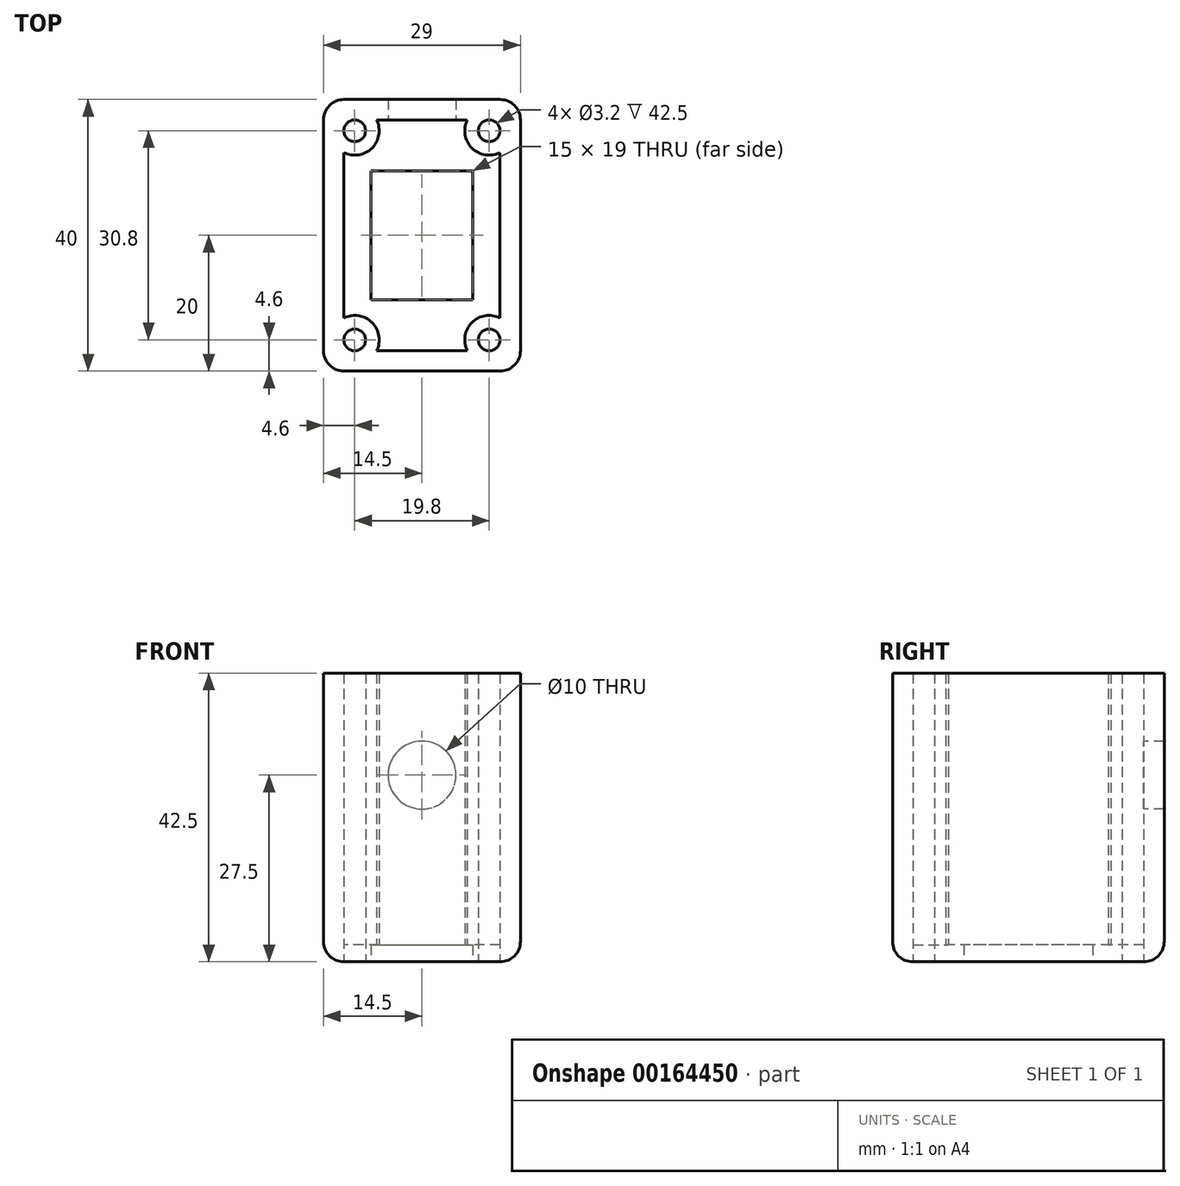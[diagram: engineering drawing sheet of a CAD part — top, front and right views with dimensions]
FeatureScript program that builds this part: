
annotation { "Feature Type Name" : "Feature", "Feature Type Description" : "" }
export const myFeature = defineFeature(function(context is Context, id is Id, definition is map)
    precondition{}
    {
        {
            var Q0;
            Q0=qCreatedBy(makeId("Top.planeOp"),FACE);
            var sketch = newSketch(context, id + "F0", { "sketchPlane" : qUnion([Q0])});
            skLineSegment(sketch, "E0.bottom", {"start": v(-14.5, 20) * mm, "end": v(14.5, 20) * mm});
            skLineSegment(sketch, "E0.top", {"start": v(-14.5, -20) * mm, "end": v(14.5, -20) * mm});
            skLineSegment(sketch, "E0.left", {"start": v(-14.5, 20) * mm, "end": v(-14.5, -20) * mm});
            skLineSegment(sketch, "E0.right", {"start": v(14.5, 20) * mm, "end": v(14.5, -20) * mm});
            skPoint(sketch, "E1", {"position": v(0, 20) * mm});
            skPoint(sketch, "E2", {"position": v(14.5, 0) * mm});
            skLineSegment(sketch, "E3.bottom", {"start": v(-7.5, 9.5) * mm, "end": v(7.5, 9.5) * mm});
            skLineSegment(sketch, "E3.top", {"start": v(-7.5, -9.5) * mm, "end": v(7.5, -9.5) * mm});
            skLineSegment(sketch, "E3.left", {"start": v(-7.5, 9.5) * mm, "end": v(-7.5, -9.5) * mm});
            skLineSegment(sketch, "E3.right", {"start": v(7.5, 9.5) * mm, "end": v(7.5, -9.5) * mm});
            skPoint(sketch, "E4", {"position": v(0, 9.5) * mm});
            skPoint(sketch, "E5", {"position": v(-7.5, 0) * mm});
            skSolve(sketch);
        }
        {
            var Q0;
            Q0=makeQuery(id+"F0.imprint","IMPRINT",FACE,{"disambiguationData":[TD([[makeQuery(id+"F0.imprint","IMPRINT",EDGE,{"derivedFrom":sQuery(id+"F0.wireOp",EDGE,"E0.bottom")}),-1.0]])]});
            extrude(context, id + "F1", {"entities" : qUnion([Q0]), "depth" : 2.5 * mm});
        }
        {
            var Q0;
            Q0=makeQuery(id+"F1.opExtrude","CAP_FACE",FACE,{"disambiguationData":[OSD([sQuery(id+"F0.wireOp",EDGE,"E0.bottom"),sQuery(id+"F0.wireOp",EDGE,"E0.top"),sQuery(id+"F0.wireOp",EDGE,"E0.left"),sQuery(id+"F0.wireOp",EDGE,"E0.right"),sQuery(id+"F0.wireOp",EDGE,"E3.bottom"),sQuery(id+"F0.wireOp",EDGE,"E3.top"),sQuery(id+"F0.wireOp",EDGE,"E3.left"),sQuery(id+"F0.wireOp",EDGE,"E3.right")])],"isStart":false});
            var sketch = newSketch(context, id + "F2", { "sketchPlane" : qUnion([Q0])});
            skLineSegment(sketch, "E6.bottom", {"start": v(-11.5, 17) * mm, "end": v(11.5, 17) * mm});
            skLineSegment(sketch, "E6.top", {"start": v(-11.5, -17) * mm, "end": v(11.5, -17) * mm});
            skLineSegment(sketch, "E6.left", {"start": v(-11.5, 17) * mm, "end": v(-11.5, -17) * mm});
            skLineSegment(sketch, "E6.right", {"start": v(11.5, 17) * mm, "end": v(11.5, -17) * mm});
            skSolve(sketch);
        }
        {
            var Q0;
            Q0=makeQuery(id+"F2.imprint","IMPRINT",FACE,{"disambiguationData":[TD([[makeQuery(id+"F2.imprint","IMPRINT",EDGE,{"derivedFrom":sQuery(id+"F2.wireOp",EDGE,"E6.bottom")}),1.0]])]});
            extrude(context, id + "F3", {"entities" : qUnion([Q0]), "operationType" : NewBodyOperationType.ADD, "depth" : 40 * mm});
        }
        {
            var Q0;
            Q0=makeQuery(id+"F1.opExtrude","CAP_FACE",FACE,{"disambiguationData":[OSD([sQuery(id+"F0.wireOp",EDGE,"E0.bottom"),sQuery(id+"F0.wireOp",EDGE,"E0.top"),sQuery(id+"F0.wireOp",EDGE,"E0.left"),sQuery(id+"F0.wireOp",EDGE,"E0.right"),sQuery(id+"F0.wireOp",EDGE,"E3.bottom"),sQuery(id+"F0.wireOp",EDGE,"E3.top"),sQuery(id+"F0.wireOp",EDGE,"E3.left"),sQuery(id+"F0.wireOp",EDGE,"E3.right")])],"isStart":false});
            var sketch = newSketch(context, id + "F4", { "sketchPlane" : qUnion([Q0])});
            skCircle(sketch, "E7", {"center": v(-9.9, 15.4) * mm, "radius": 3.6 * mm});
            skCircle(sketch, "E8", {"center": v(9.9, 15.4) * mm, "radius": 3.6 * mm});
            skCircle(sketch, "E9", {"center": v(9.9, -15.4) * mm, "radius": 3.6 * mm});
            skCircle(sketch, "E10", {"center": v(-9.9, -15.4) * mm, "radius": 3.6 * mm});
            skCircle(sketch, "E11", {"center": v(-9.9, 15.4) * mm, "radius": 1.6 * mm});
            skCircle(sketch, "E12", {"center": v(9.9, 15.4) * mm, "radius": 1.6 * mm});
            skCircle(sketch, "E13", {"center": v(-9.9, -15.4) * mm, "radius": 1.6 * mm});
            skCircle(sketch, "E14", {"center": v(9.9, -15.4) * mm, "radius": 1.6 * mm});
            skSolve(sketch);
        }
        {
            var Q0;
            {var subQ0=sQuery(id+"F4.wireOp",EDGE,"E7");var subQ1=makeQuery(id+"F3.opExtrude","CAP_EDGE",EDGE,{"disambiguationData":[OSD([sQuery(id+"F2.wireOp",EDGE,"E6.bottom")])],"isStart":true});var subQ2=makeQuery(id+"F4.imprint","INTERSECT",VERTEX,{"derivedFrom":[subQ1,subQ0]});Q0=makeQuery(id+"F4.imprint","IMPRINT",FACE,{"disambiguationData":[TD([[makeQuery(id+"F4.imprint","IMPRINT",EDGE,{"disambiguationData":[TD([[subQ2,1.0]])],"derivedFrom":subQ0}),1.0]])]});}
            var Q1;
            {var subQ0=sQuery(id+"F4.wireOp",EDGE,"E11");var subQ1=makeQuery(id+"F3.opExtrude","CAP_EDGE",EDGE,{"disambiguationData":[OSD([sQuery(id+"F2.wireOp",EDGE,"E6.bottom")])],"isStart":true});var subQ2=makeQuery(id+"F4.imprint","INTERSECT",VERTEX,{"derivedFrom":[subQ1,subQ0]});Q1=makeQuery(id+"F4.imprint","IMPRINT",FACE,{"disambiguationData":[TD([[makeQuery(id+"F4.imprint","IMPRINT",EDGE,{"disambiguationData":[TD([[subQ2,-1.0]])],"derivedFrom":subQ0}),-1.0]])]});}
            var Q2;
            {var subQ0=sQuery(id+"F4.wireOp",EDGE,"E8");var subQ1=makeQuery(id+"F3.opExtrude","CAP_EDGE",EDGE,{"disambiguationData":[OSD([sQuery(id+"F2.wireOp",EDGE,"E6.bottom")])],"isStart":true});var subQ2=makeQuery(id+"F4.imprint","INTERSECT",VERTEX,{"derivedFrom":[subQ1,subQ0]});Q2=makeQuery(id+"F4.imprint","IMPRINT",FACE,{"disambiguationData":[TD([[makeQuery(id+"F4.imprint","IMPRINT",EDGE,{"disambiguationData":[TD([[subQ2,-1.0]])],"derivedFrom":subQ0}),1.0]])]});}
            var Q3;
            {var subQ0=sQuery(id+"F4.wireOp",EDGE,"E12");var subQ1=makeQuery(id+"F3.opExtrude","CAP_EDGE",EDGE,{"disambiguationData":[OSD([sQuery(id+"F2.wireOp",EDGE,"E6.bottom")])],"isStart":true});var subQ2=makeQuery(id+"F4.imprint","INTERSECT",VERTEX,{"derivedFrom":[subQ1,subQ0]});Q3=makeQuery(id+"F4.imprint","IMPRINT",FACE,{"disambiguationData":[TD([[makeQuery(id+"F4.imprint","IMPRINT",EDGE,{"disambiguationData":[TD([[subQ2,1.0]])],"derivedFrom":subQ0}),-1.0]])]});}
            var Q4;
            {var subQ0=sQuery(id+"F4.wireOp",EDGE,"E13");var subQ1=makeQuery(id+"F3.opExtrude","CAP_EDGE",EDGE,{"disambiguationData":[OSD([sQuery(id+"F2.wireOp",EDGE,"E6.top")])],"isStart":true});var subQ2=makeQuery(id+"F4.imprint","INTERSECT",VERTEX,{"derivedFrom":[subQ1,subQ0]});Q4=makeQuery(id+"F4.imprint","IMPRINT",FACE,{"disambiguationData":[TD([[makeQuery(id+"F4.imprint","IMPRINT",EDGE,{"disambiguationData":[TD([[subQ2,1.0]])],"derivedFrom":subQ0}),-1.0]])]});}
            var Q5;
            {var subQ0=sQuery(id+"F4.wireOp",EDGE,"E10");var subQ1=makeQuery(id+"F3.opExtrude","CAP_EDGE",EDGE,{"disambiguationData":[OSD([sQuery(id+"F2.wireOp",EDGE,"E6.top")])],"isStart":true});var subQ2=makeQuery(id+"F4.imprint","INTERSECT",VERTEX,{"derivedFrom":[subQ1,subQ0]});Q5=makeQuery(id+"F4.imprint","IMPRINT",FACE,{"disambiguationData":[TD([[makeQuery(id+"F4.imprint","IMPRINT",EDGE,{"disambiguationData":[TD([[subQ2,-1.0]])],"derivedFrom":subQ0}),1.0]])]});}
            var Q6;
            {var subQ0=sQuery(id+"F4.wireOp",EDGE,"E9");var subQ1=makeQuery(id+"F3.opExtrude","CAP_EDGE",EDGE,{"disambiguationData":[OSD([sQuery(id+"F2.wireOp",EDGE,"E6.top")])],"isStart":true});var subQ2=makeQuery(id+"F4.imprint","INTERSECT",VERTEX,{"derivedFrom":[subQ1,subQ0]});Q6=makeQuery(id+"F4.imprint","IMPRINT",FACE,{"disambiguationData":[TD([[makeQuery(id+"F4.imprint","IMPRINT",EDGE,{"disambiguationData":[TD([[subQ2,1.0]])],"derivedFrom":subQ0}),1.0]])]});}
            var Q7;
            {var subQ0=sQuery(id+"F4.wireOp",EDGE,"E14");var subQ1=makeQuery(id+"F3.opExtrude","CAP_EDGE",EDGE,{"disambiguationData":[OSD([sQuery(id+"F2.wireOp",EDGE,"E6.top")])],"isStart":true});var subQ2=makeQuery(id+"F4.imprint","INTERSECT",VERTEX,{"derivedFrom":[subQ1,subQ0]});Q7=makeQuery(id+"F4.imprint","IMPRINT",FACE,{"disambiguationData":[TD([[makeQuery(id+"F4.imprint","IMPRINT",EDGE,{"disambiguationData":[TD([[subQ2,-1.0]])],"derivedFrom":subQ0}),-1.0]])]});}
            var Q8;
            Q8=makeQuery(id+"F3.opExtrude","CAP_FACE",FACE,{"disambiguationData":[OSD([sQuery(id+"F0.wireOp",EDGE,"E0.bottom"),sQuery(id+"F0.wireOp",EDGE,"E0.top"),sQuery(id+"F0.wireOp",EDGE,"E0.left"),sQuery(id+"F0.wireOp",EDGE,"E0.right"),sQuery(id+"F2.wireOp",EDGE,"E6.bottom"),sQuery(id+"F2.wireOp",EDGE,"E6.top"),sQuery(id+"F2.wireOp",EDGE,"E6.left"),sQuery(id+"F2.wireOp",EDGE,"E6.right")])],"isStart":false});
            extrude(context, id + "F5", {"entities" : qUnion([Q0, Q1, Q2, Q3, Q4, Q5, Q6, Q7]), "operationType" : NewBodyOperationType.ADD, "endBound" : BoundingType.UP_TO_SURFACE, "endBoundEntityFace" : qUnion([Q8]), "depth" : 25 * mm});
        }
        {
            var Q0;
            Q0=makeQuery(id+"F1.opExtrude","CAP_FACE",FACE,{"disambiguationData":[OSD([sQuery(id+"F0.wireOp",EDGE,"E0.bottom"),sQuery(id+"F0.wireOp",EDGE,"E0.top"),sQuery(id+"F0.wireOp",EDGE,"E0.left"),sQuery(id+"F0.wireOp",EDGE,"E0.right"),sQuery(id+"F0.wireOp",EDGE,"E3.bottom"),sQuery(id+"F0.wireOp",EDGE,"E3.top"),sQuery(id+"F0.wireOp",EDGE,"E3.left"),sQuery(id+"F0.wireOp",EDGE,"E3.right")])],"isStart":true});
            var sketch = newSketch(context, id + "F6", { "sketchPlane" : qUnion([Q0])});
            skCircle(sketch, "E15", {"center": v(-9.9, 15.4) * mm, "radius": 1.6 * mm});
            skCircle(sketch, "E16", {"center": v(9.9, 15.4) * mm, "radius": 1.6 * mm});
            skCircle(sketch, "E17", {"center": v(9.9, -15.4) * mm, "radius": 1.6 * mm});
            skCircle(sketch, "E18", {"center": v(-9.9, -15.4) * mm, "radius": 1.6 * mm});
            skSolve(sketch);
        }
        {
            var Q0;
            Q0=makeQuery(id+"F6.imprint","IMPRINT",FACE,{"disambiguationData":[TD([[makeQuery(id+"F6.imprint","IMPRINT",EDGE,{"derivedFrom":sQuery(id+"F6.wireOp",EDGE,"E15")}),1.0]])]});
            var Q1;
            Q1=makeQuery(id+"F6.imprint","IMPRINT",FACE,{"disambiguationData":[TD([[makeQuery(id+"F6.imprint","IMPRINT",EDGE,{"derivedFrom":sQuery(id+"F6.wireOp",EDGE,"E16")}),1.0]])]});
            var Q2;
            Q2=makeQuery(id+"F6.imprint","IMPRINT",FACE,{"disambiguationData":[TD([[makeQuery(id+"F6.imprint","IMPRINT",EDGE,{"derivedFrom":sQuery(id+"F6.wireOp",EDGE,"E17")}),1.0]])]});
            var Q3;
            Q3=makeQuery(id+"F6.imprint","IMPRINT",FACE,{"disambiguationData":[TD([[makeQuery(id+"F6.imprint","IMPRINT",EDGE,{"derivedFrom":sQuery(id+"F6.wireOp",EDGE,"E18")}),1.0]])]});
            extrude(context, id + "F7", {"entities" : qUnion([Q0, Q1, Q2, Q3]), "operationType" : NewBodyOperationType.REMOVE, "oppositeDirection" : true, "depth" : 25 * mm});
        }
        {
            var Q0;
            {var subQ0=sQuery(id+"F0.wireOp",EDGE,"E0.left");var subQ1=sQuery(id+"F0.wireOp",EDGE,"E0.top");Q0=makeQuery(id+"F3.boolean.opBoolean","MERGE",EDGE,{"derivedFrom":[makeQuery(id+"F1.opExtrude","SWEPT_EDGE",EDGE,{"disambiguationData":[OSD([subQ1,subQ0])]}),makeQuery(id+"F3.opExtrude","SWEPT_EDGE",EDGE,{"disambiguationData":[OSD([subQ1,subQ0])]})]});}
            var Q1;
            {var subQ0=sQuery(id+"F0.wireOp",EDGE,"E0.right");var subQ1=sQuery(id+"F0.wireOp",EDGE,"E0.top");Q1=makeQuery(id+"F3.boolean.opBoolean","MERGE",EDGE,{"derivedFrom":[makeQuery(id+"F1.opExtrude","SWEPT_EDGE",EDGE,{"disambiguationData":[OSD([subQ1,subQ0])]}),makeQuery(id+"F3.opExtrude","SWEPT_EDGE",EDGE,{"disambiguationData":[OSD([subQ1,subQ0])]})]});}
            var Q2;
            {var subQ0=sQuery(id+"F0.wireOp",EDGE,"E0.left");var subQ1=sQuery(id+"F0.wireOp",EDGE,"E0.bottom");Q2=makeQuery(id+"F3.boolean.opBoolean","MERGE",EDGE,{"derivedFrom":[makeQuery(id+"F1.opExtrude","SWEPT_EDGE",EDGE,{"disambiguationData":[OSD([subQ1,subQ0])]}),makeQuery(id+"F3.opExtrude","SWEPT_EDGE",EDGE,{"disambiguationData":[OSD([subQ1,subQ0])]})]});}
            var Q3;
            {var subQ0=sQuery(id+"F0.wireOp",EDGE,"E0.right");var subQ1=sQuery(id+"F0.wireOp",EDGE,"E0.bottom");Q3=makeQuery(id+"F3.boolean.opBoolean","MERGE",EDGE,{"derivedFrom":[makeQuery(id+"F1.opExtrude","SWEPT_EDGE",EDGE,{"disambiguationData":[OSD([subQ1,subQ0])]}),makeQuery(id+"F3.opExtrude","SWEPT_EDGE",EDGE,{"disambiguationData":[OSD([subQ1,subQ0])]})]});}
            var Q4;
            Q4=makeQuery(id+"F1.opExtrude","CAP_EDGE",EDGE,{"disambiguationData":[OSD([sQuery(id+"F0.wireOp",EDGE,"E0.left")])],"isStart":true});
            var Q5;
            Q5=makeQuery(id+"F1.opExtrude","CAP_EDGE",EDGE,{"disambiguationData":[OSD([sQuery(id+"F0.wireOp",EDGE,"E0.bottom")])],"isStart":true});
            var Q6;
            Q6=makeQuery(id+"F1.opExtrude","CAP_EDGE",EDGE,{"disambiguationData":[OSD([sQuery(id+"F0.wireOp",EDGE,"E0.right")])],"isStart":true});
            var Q7;
            Q7=makeQuery(id+"F1.opExtrude","CAP_EDGE",EDGE,{"disambiguationData":[OSD([sQuery(id+"F0.wireOp",EDGE,"E0.top")])],"isStart":true});
            fillet(context, id + "F8", {"entities" : qUnion([Q0, Q1, Q2, Q3, Q4, Q5, Q6, Q7]), "radius" : 3 * mm, "tangentPropagation" : true, "allowEdgeOverflow" : false});
        }
        {
            var Q0;
            Q0=makeQuery(id+"F3.opExtrude","SWEPT_FACE",FACE,{"disambiguationData":[OSD([sQuery(id+"F2.wireOp",EDGE,"E6.bottom")])]});
            var sketch = newSketch(context, id + "F9", { "sketchPlane" : qUnion([Q0])});
            skCircle(sketch, "E19", {"center": v(0, 27.5) * mm, "radius": 5 * mm});
            skLineSegment(sketch, "E20", {"start": v(-6.68, 42.5) * mm, "end": v(6.68, 42.5) * mm});
            skPoint(sketch, "E21", {"position": v(0, 42.5) * mm});
            skSolve(sketch);
        }
        {
            var Q0;
            Q0=makeQuery(id+"F9.imprint","IMPRINT",FACE,{"disambiguationData":[TD([[makeQuery(id+"F9.imprint","IMPRINT",EDGE,{"derivedFrom":sQuery(id+"F9.wireOp",EDGE,"E19")}),1.0]])]});
            extrude(context, id + "F10", {"entities" : qUnion([Q0]), "operationType" : NewBodyOperationType.REMOVE, "endBound" : BoundingType.UP_TO_NEXT, "oppositeDirection" : true, "depth" : 25 * mm});
        }
    });
